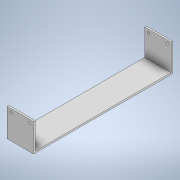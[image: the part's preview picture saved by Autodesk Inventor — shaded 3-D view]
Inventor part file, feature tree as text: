
AUTODESK INVENTOR PART (.ipt)
format: ipt  version: 2020 (Build 240168000, 168)  size: 126,464 bytes
history: native  units: in
note: dims shown in document units (in); Inventor stores cm internally (conversion verified against a paired STEP export)
features: extrude x3, sketch x3
ambient origin geometry x8: Origin, YZ Plane, XZ Plane, XY Plane, X Axis, Y Axis, Z Axis, Center Point
bodies: Solid1 (feature_tree)
feature tree (6):
  extrude  "Extrusion1"  Depth=1.5in
  extrude  "Extrusion2"  Depth=1.5in TaperAngle=0.0deg
  extrude  "Extrusion3"  Depth=1.061in
  sketch  "Sketch1"  dims[d0=7.925in d1=1.5in]
  sketch  "Sketch2"  dims[d2=0.1in d3=0.0in d4=1.5in d5=0.0in]
  sketch  "Sketch3"  dims[d9=9.6875in d10=0.0in d11=1.061in d12=0.141in d13=0.141in]
